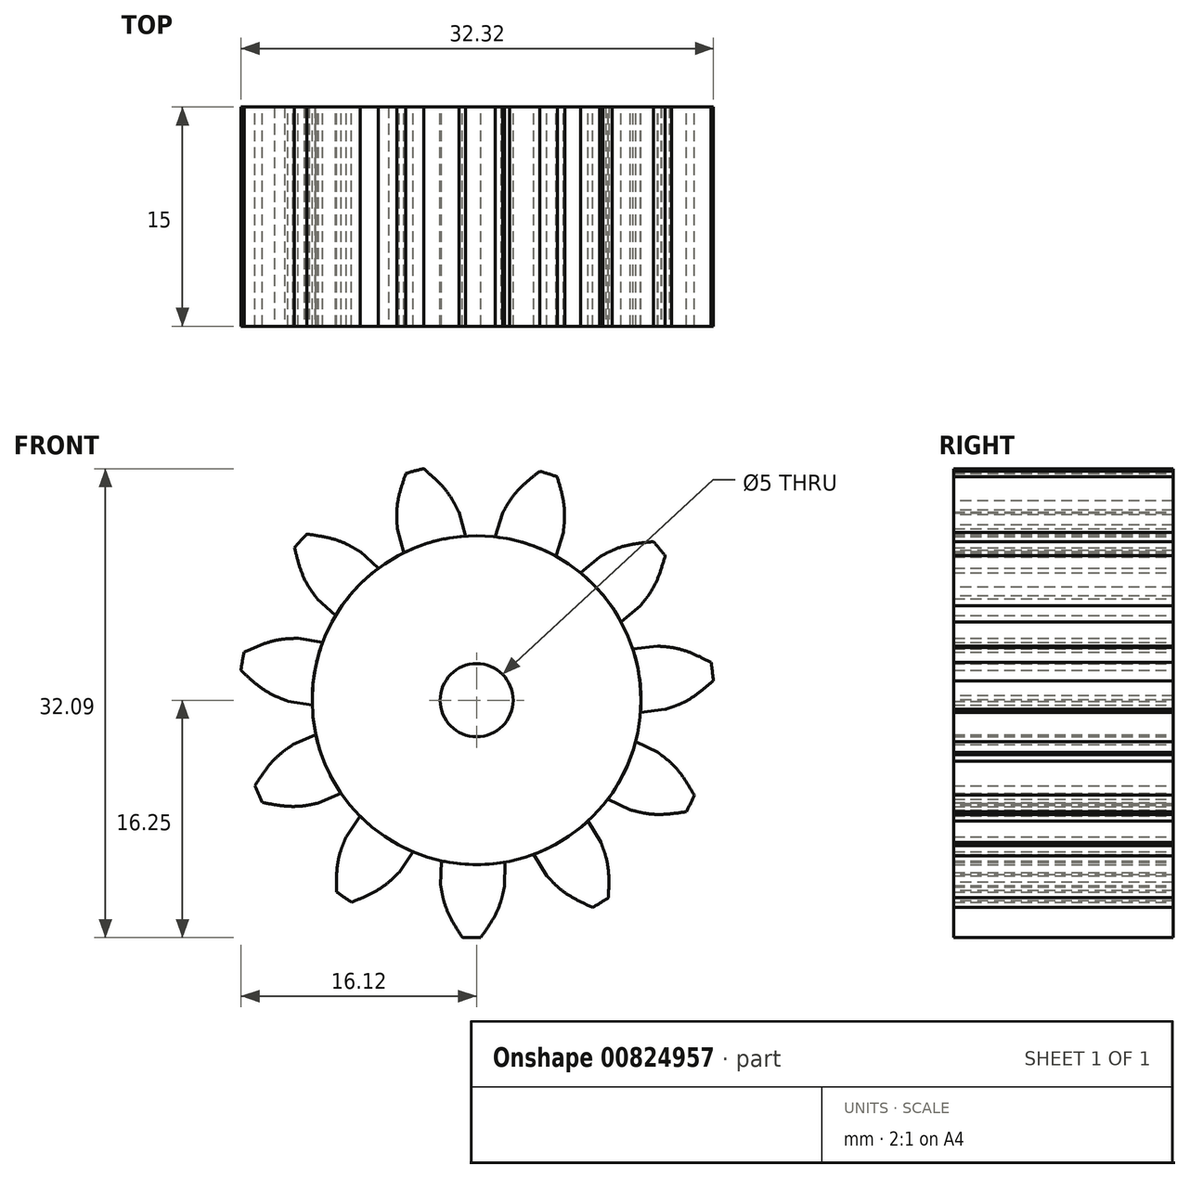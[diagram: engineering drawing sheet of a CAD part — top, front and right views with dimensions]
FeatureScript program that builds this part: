
annotation { "Feature Type Name" : "Feature", "Feature Type Description" : "" }
export const myFeature = defineFeature(function(context is Context, id is Id, definition is map)
    precondition{}
    {
        {
            var Q0;
            Q0=qCreatedBy(makeId("Front.planeOp"),FACE);
            var sketch = newSketch(context, id + "F0", { "sketchPlane" : qUnion([Q0])});
            skCircle(sketch, "E0", {"center": v(0, 0) * mm, "radius": 13.75 * mm, "construction": true});
            skCircle(sketch, "E1", {"center": v(0, 0) * mm, "radius": 16.25 * mm});
            skCircle(sketch, "E2", {"center": v(0, 0) * mm, "radius": 11.25 * mm});
            skCircle(sketch, "E3", {"center": v(0, 0) * mm, "radius": 12.92 * mm, "construction": true});
            skLineSegment(sketch, "E4", {"start": v(-2.95, 13.75) * mm, "end": v(3.28, 13.75) * mm});
            skPoint(sketch, "E5", {"position": v(0, 13.75) * mm});
            skLineSegment(sketch, "E6", {"start": v(4.42, 12.14) * mm, "end": v(-4.84, 15.51) * mm});
            skLineSegment(sketch, "E7", {"start": v(0, 0) * mm, "end": v(4.42, 12.14) * mm, "construction": true});
            skPoint(sketch, "E8", {"position": v(-5.43, 11.73) * mm});
            skLineSegment(sketch, "E9", {"start": v(-5.43, 11.73) * mm, "end": v(0, 0) * mm, "construction": true});
            skLineSegment(sketch, "E10", {"start": v(0, 0) * mm, "end": v(1.97, 12.77) * mm, "construction": true});
            skLineSegment(sketch, "E11", {"start": v(0, 0) * mm, "end": v(-0.55, 12.9) * mm, "construction": true});
            skLineSegment(sketch, "E12", {"start": v(0, 0) * mm, "end": v(-3.04, 12.56) * mm, "construction": true});
            skLineSegment(sketch, "E13", {"start": v(-3.04, 12.56) * mm, "end": v(-5.44, 11.98) * mm});
            skLineSegment(sketch, "E14", {"start": v(-0.55, 12.9) * mm, "end": v(-5.47, 12.7) * mm});
            skLineSegment(sketch, "E15", {"start": v(1.97, 12.77) * mm, "end": v(-5.33, 13.9) * mm});
            skFitSpline(sketch, "E16", {"points": [v(-5.43, 11.73) * mm, v(-5.44, 11.98) * mm, v(-5.47, 12.7) * mm, v(-5.33, 13.9) * mm, v(-4.84, 15.51) * mm], "startDerivative": vector(-0.06, 1.65) * mm, "endDerivative": vector(1.63, 4.78) * mm});
            skLineSegment(sketch, "E17", {"start": v(0, 0) * mm, "end": v(-4.24, 15.69) * mm, "construction": true});
            skLineSegment(sketch, "E18", {"start": v(-5.47, 12.7) * mm, "end": v(0, 0) * mm, "construction": true});
            skLineSegment(sketch, "E19", {"start": v(-5.43, 11.73) * mm, "end": v(-4.98, 10.09) * mm});
            skFitSpline(sketch, "E20.MirrorCS", {"points": [v(-1.21, 12.86) * mm, v(-1.33, 13.09) * mm, v(-1.67, 13.73) * mm, v(-2.4, 14.7) * mm, v(-3.63, 15.84) * mm], "startDerivative": vector(-0.78, 1.46) * mm, "endDerivative": vector(-3.81, 3.31) * mm});
            skLineSegment(sketch, "E21.MirrorCS", {"start": v(-1.21, 12.86) * mm, "end": v(-0.77, 11.22) * mm});
            skSolve(sketch);
        }
        {
            var Q0;
            {var subQ0=sQuery(id+"F0.wireOp",EDGE,"E2");var subQ1=makeQuery(id+"F0.imprint","INTERSECT",VERTEX,{"derivedFrom":[subQ0,sQuery(id+"F0.wireOp",EDGE,"E19")]});Q0=makeQuery(id+"F0.imprint","IMPRINT",FACE,{"disambiguationData":[TD([[makeQuery(id+"F0.imprint","IMPRINT",EDGE,{"disambiguationData":[TD([[subQ1,1.0]])],"derivedFrom":subQ0}),1.0]])]});}
            extrude(context, id + "F1", {"entities" : qUnion([Q0]), "depth" : 15 * mm, "offsetDistance" : 25 * mm});
        }
        {
            var Q0;
            {var subQ1=sQuery(id+"F0.wireOp",EDGE,"E1");var subQ3=sQuery(id+"F0.wireOp",EDGE,"E20.MirrorCS");var subQ4=makeQuery(id+"F0.imprint","INTERSECT",VERTEX,{"derivedFrom":[subQ1,subQ3]});Q0=makeQuery(id+"F0.imprint","IMPRINT",FACE,{"disambiguationData":[TD([[makeQuery(id+"F0.imprint","IMPRINT",EDGE,{"disambiguationData":[TD([[subQ4,1.0]])],"derivedFrom":subQ3}),1.0]])]});}
            var Q1;
            {var subQ0=sQuery(id+"F0.wireOp",EDGE,"E16");var subQ3=sQuery(id+"F0.wireOp",EDGE,"E15");var subQ4=makeQuery(id+"F0.imprint","INTERSECT",VERTEX,{"derivedFrom":[subQ3,subQ0]});Q1=makeQuery(id+"F0.imprint","IMPRINT",FACE,{"disambiguationData":[TD([[makeQuery(id+"F0.imprint","IMPRINT",EDGE,{"disambiguationData":[TD([[subQ4,1.0]])],"derivedFrom":subQ3}),-1.0]])]});}
            var Q2;
            {var subQ0=sQuery(id+"F0.wireOp",EDGE,"E16");var subQ1=sQuery(id+"F0.wireOp",EDGE,"E14");var subQ2=makeQuery(id+"F0.imprint","INTERSECT",VERTEX,{"derivedFrom":[subQ1,subQ0]});Q2=makeQuery(id+"F0.imprint","IMPRINT",FACE,{"disambiguationData":[TD([[makeQuery(id+"F0.imprint","IMPRINT",EDGE,{"disambiguationData":[TD([[subQ2,1.0]])],"derivedFrom":subQ1}),-1.0]])]});}
            var Q3;
            {var subQ4=sQuery(id+"F0.wireOp",EDGE,"E19");Q3=makeQuery(id+"F0.imprint","IMPRINT",FACE,{"disambiguationData":[TD([[makeQuery(id+"F0.imprint","IMPRINT",EDGE,{"derivedFrom":subQ4}),1.0]])]});}
            extrude(context, id + "F2", {"entities" : qUnion([Q0, Q1, Q2, Q3]), "depth" : 15 * mm, "offsetDistance" : 25 * mm});
        }
        {
            var Q0;
            Q0=qCreatedBy(makeId("Right.planeOp"),FACE);
            var sketch = newSketch(context, id + "F3", { "sketchPlane" : qUnion([Q0])});
            skLineSegment(sketch, "E22", {"start": v(0, 0) * mm, "end": v(-53.35, 0) * mm});
            skSolve(sketch);
        }
        {
            var Q0;
            Q0=makeQuery(id+"F2.opExtrude","SWEPT_BODY",BODY,{"disambiguationData":[OSD([sQuery(id+"F0.wireOp",EDGE,"E1"),sQuery(id+"F0.wireOp",EDGE,"E2"),sQuery(id+"F0.wireOp",EDGE,"E16"),sQuery(id+"F0.wireOp",EDGE,"E19"),sQuery(id+"F0.wireOp",EDGE,"E20.MirrorCS"),sQuery(id+"F0.wireOp",EDGE,"E21.MirrorCS")])]});
            var Q1;
            Q1=sQuery(id+"F3.wireOp",EDGE,"E22");
            circularPattern(context, id + "F4", {"entities" : qUnion([Q0]), "axis" : qUnion([Q1]), "angle" : 360 * degree, "instanceCount" : 11, "equalSpace" : true});
        }
        {
            var Q0;
            Q0=qCreatedBy(makeId("Front.planeOp"),FACE);
            var sketch = newSketch(context, id + "F5", { "sketchPlane" : qUnion([Q0])});
            skCircle(sketch, "E23", {"center": v(0, 0) * mm, "radius": 2.5 * mm});
            skSolve(sketch);
        }
        {
            var Q0;
            Q0 = qSketchRegion(id + "F5", true);
            extrude(context, id + "F6", {"entities" : qUnion([Q0]), "operationType" : NewBodyOperationType.REMOVE, "endBound" : BoundingType.THROUGH_ALL, "depth" : 25 * mm, "offsetDistance" : 25 * mm});
        }
    });
